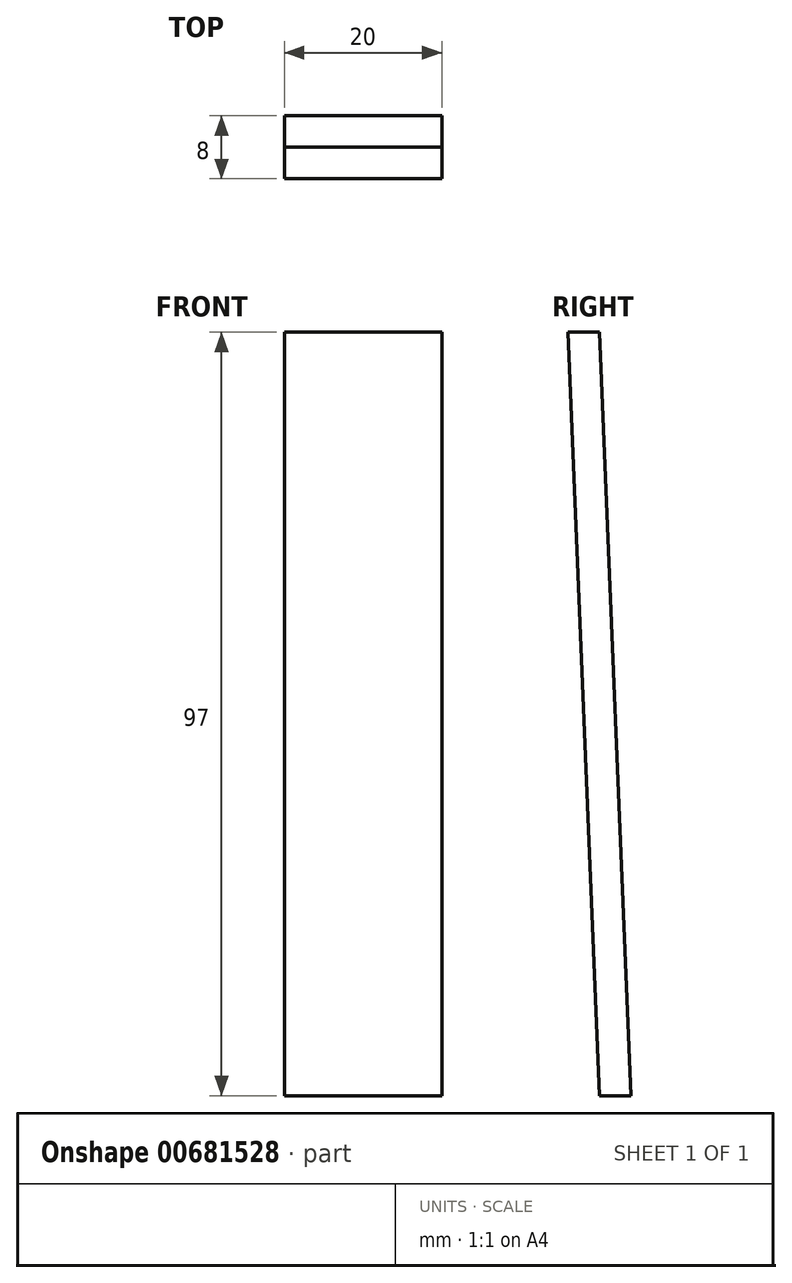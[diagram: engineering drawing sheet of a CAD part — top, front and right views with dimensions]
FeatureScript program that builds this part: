
annotation { "Feature Type Name" : "Feature", "Feature Type Description" : "" }
export const myFeature = defineFeature(function(context is Context, id is Id, definition is map)
    precondition{}
    {
        {
            var Q0;
            Q0=qCreatedBy(makeId("Right.planeOp"),FACE);
            var sketch = newSketch(context, id + "F0", { "sketchPlane" : qUnion([Q0])});
            skLineSegment(sketch, "E0.bottom", {"start": v(0, 0) * mm, "end": v(-8, 0) * mm});
            skLineSegment(sketch, "E0.top", {"start": v(0, 97) * mm, "end": v(-8, 97) * mm});
            skLineSegment(sketch, "E0.left", {"start": v(0, 0) * mm, "end": v(0, 97) * mm});
            skLineSegment(sketch, "E0.right", {"start": v(-8, 0) * mm, "end": v(-8, 97) * mm});
            skLineSegment(sketch, "E1", {"start": v(-8, 97) * mm, "end": v(-4, 0) * mm});
            skLineSegment(sketch, "E2", {"start": v(0, 0) * mm, "end": v(-4, 97) * mm});
            skSolve(sketch);
        }
        {
            var Q0;
            {var subQ2=sQuery(id+"F0.wireOp",EDGE,"E1");Q0=makeQuery(id+"F0.imprint","IMPRINT",FACE,{"disambiguationData":[TD([[makeQuery(id+"F0.imprint","IMPRINT",EDGE,{"derivedFrom":subQ2}),1.0]])]});}
            extrude(context, id + "F1", {"entities" : qUnion([Q0]), "depth" : 20 * mm, "offsetDistance" : 25 * mm});
        }
    });
